# Revit family: Solar LED
name_source: partatom
category: Lighting Fixtures
revit_build: Autodesk Revit 2016 (Build: 20150714_1515(x64)
units: mm (PartAtom-declared; Revit-internal decimal feet)

## family parameters
Cut with Voids When Loaded = Yes
Host = Face
Light Source = Yes
Part Type = Normal
Room Calculation Point = No
Round Connector Dimension = Use Diameter
Shared = No

## types (1)
- Solar LED
    Apparent Load = 0 VA
    Assembly Code = SGL/LED/4/XXXX/SOL
    Classification.Uniclass.Pr.Description = Surface luminaires
    Classification.Uniclass.Pr.Number = Pr_70_70_48_85
    Color Filter = 16777215
    Default Elevation = 1200 mm
    Depth = 33 mm  [stored 0.108268 ft]
    Description = LED Surface
    Dimming Lamp Color Temperature Shift = <None>
    Emit Shape Visible in Rendering = No
    Emit from Circle Diameter = 340 mm
    Lamp = LED
    Light Source Symbol Size = 610 mm
    Manufacturer = Southgate Lighting
    Middle Height = 280 mm
    Model = Solar LED
    Type Image = <None>
    URL = www.southgatelighting.com
    Width = 400 mm

note: [stored X ft] marks values corroborated as IEEE doubles in the binary element streams (Revit-internal decimal feet)

## geometry (parser evidence)
native form markers: Sweep x3
no freeform markers — native parametric forms only
